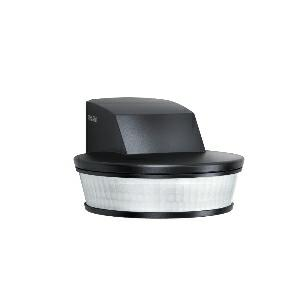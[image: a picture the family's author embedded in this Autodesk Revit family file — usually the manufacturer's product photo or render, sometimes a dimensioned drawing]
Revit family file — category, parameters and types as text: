
# Revit family: sensiq_s_034979
name_source: partatom
category: Elektroinstallationen
revit_build: Autodesk Revit 2016 (Build: 20190508_0715(x64)
units: mm (PartAtom-declared; Revit-internal decimal feet)

## family parameters
Basisbauteil = Fläche
Beim Laden mit Abzugskörper schneiden = Nein
Bemaßung runder Anschluss = Durchmesser verwenden
Beschriftungsausrichtung beibehalten = Nein
Gemeinsam genutzt = Nein
Raumberechnungspunkt = Nein
Teiletyp = Normal

## types (1)
- sensIQ S
    Apparent Load = 0 VA
    Beschreibung = Type: Motion detectors; Type of accessory: Corner adapter; Dimensions (L x W x H): 128 x 114 x 74 mm; Mains power supply: 100 – 240 V / 50 – 60 Hz; Power supply, detail: 500 VA max., 120 V; Sensor Technology: passive infrared; Application, place: Indoors, Outdoors; Application, room: multi-storey / underground car park, outdoors, warehouse, front door, all round the building, courtyard & driveway, Indoors; Installation site: wall, corner; Installation: Surface wiring; Switching zones: 1360 switching zones; Electronic scalability: No; Mechanical scalability: Yes; Mounting height: 2,00 – 5,00 m; Optimum mounting height: 2 m; Detection angle: 300 °; Angle of aperture: 90 °; Sneak-by guard: Yes; Capability of masking out individual segments: Yes; Reach, detail: Reach adjustable from 2 - 20 m in 3 directions (100° in each); Reach, radial: r = 4 m (42 m²); Reach, tangential: r = 20 m (1047 m²); Twilight setting TEACH: Yes; Twilight setting: 2 – 2000 lx; Time setting: 5 sec – 15 min; Switching output 1, resistive: 2000 W; Constant-lighting control: No; Basic light level function: No; Functions: Normal / test mode, Manual ON / ON-OFF; Settings via: Remote control, Potentiometers, Smart Remote; With remote control: Yes; Interconnection: Yes; IP-rating: IP54; Material: Plastic; Ambient temperature: -20 – 50 °C; Colour: black; Colour, RAL: 9005; IDs, certificates: VDE; Manufacturer's Warranty: 5 years; Version: black; PU1, EAN: 4007841034979
    Height = 74 mm
    Hersteller = Steinel
    Length = 128 mm
    Maximum range = 22.149 m
    ModVariant = Nein
    Modell = 034979
    Mounting Type = Surface mounted
    Number of Poles = 1
    OnlyDefault = Ja
    Power Factor = 1
    Product Name = sensIQ S
    Product group = Sensor-switched indoor light
    ProductGroupID = 30
    Protection Class = Protection class
    Protection Degree = IP 54
    RlxData = <blob elided: 171917 chars, md5=6dd4c38d>
    Sensor characteristics = Semi circular 145°-300°
    Sensor type = Passive (infrared)
    SensorDataFile = <blob elided: 9086 chars, md5=cfd8d4b9>
    Type of entry = Motion
    Typenbild = produkt1_034979.jpg
    Typenkommentare = Product without accessories
    URL = http://relux.com
    VarID = ---
    Voltage = 0 V
    Vorgabe-Ansicht = 1800 mm
    Weight = 0.00 kg
    Width = 114 mm

## geometry (parser evidence)
native form markers: Sweep x19
no freeform markers — native parametric forms only
